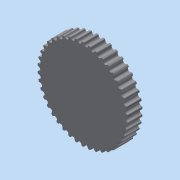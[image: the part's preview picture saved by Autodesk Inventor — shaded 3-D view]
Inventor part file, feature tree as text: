
AUTODESK INVENTOR PART (.ipt)
format: ipt  version: 2015 (Build 190159000, 159)  size: 435,200 bytes
history: native  units: in
note: dims shown in document units (in); Inventor stores cm internally (conversion verified against a paired STEP export)
features: other x2, direct_edit x2, extrude x1, pattern_circular x1, imported_body x1, sketch x1, projected_geometry x1, move_body x1
ambient origin geometry x8: Origin, YZ Plane, XZ Plane, XY Plane, X Axis, Y Axis, Z Axis, Center Point
bodies: Solid1 (feature_tree)
feature tree (10):
  other  "a_6a24m042tm201"
  direct_edit  "Direct Edit1"
  direct_edit  "Direct Edit2"
  extrude  "Extrusion1"  Depth=0.3937in TaperAngle=360.0deg
  pattern_circular  "Circular Pattern1"  [2 undecoded]
  imported_body  "Base1"
  sketch  "Sketch1"  dims[d0=0.0in d1=0.0in d2=-7.4567in d7=16.5354in d9=360.0deg d11=0.3937in d12=0.0in d13=16.5354in d14=360.0deg]
  projected_geometry  "Projected Loop1"
  move_body  "Move1"
  other  "Delete1"
note: 2 required parameter values undecoded (feature->parameter linkage not recoverable at this tier; creation-order binding heuristic only, values carry confidence <= 0.55)
